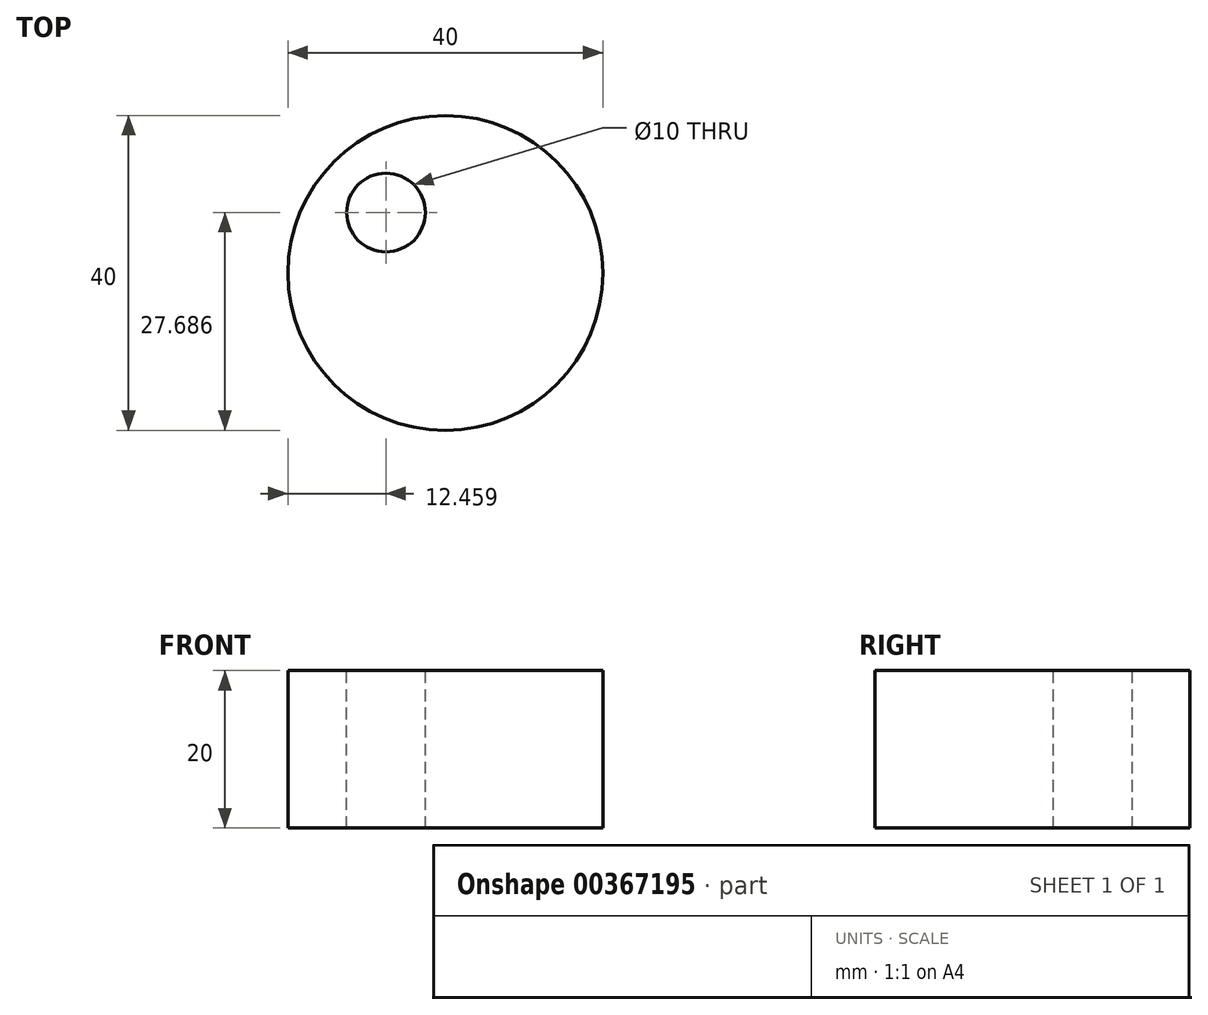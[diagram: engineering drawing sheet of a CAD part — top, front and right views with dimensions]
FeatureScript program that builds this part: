
annotation { "Feature Type Name" : "Feature", "Feature Type Description" : "" }
export const myFeature = defineFeature(function(context is Context, id is Id, definition is map)
    precondition{}
    {
        {
            var Q0;
            Q0=qCreatedBy(makeId("Front.planeOp"),FACE);
            var sketch = newSketch(context, id + "F0", { "sketchPlane" : qUnion([Q0])});
            skLineSegment(sketch, "E0.bottom", {"start": v(0, 0) * mm, "end": v(20, 0) * mm});
            skLineSegment(sketch, "E0.top", {"start": v(0, 20) * mm, "end": v(20, 20) * mm});
            skLineSegment(sketch, "E0.left", {"start": v(0, 0) * mm, "end": v(0, 20) * mm});
            skLineSegment(sketch, "E0.right", {"start": v(20, 0) * mm, "end": v(20, 20) * mm});
            skSolve(sketch);
        }
        {
            var Q0;
            Q0=makeQuery(id+"F0.imprint","IMPRINT",FACE,{"disambiguationData":[TD([[makeQuery(id+"F0.imprint","IMPRINT",EDGE,{"derivedFrom":sQuery(id+"F0.wireOp",EDGE,"E0.bottom")}),1.0]])]});
            var Q1;
            Q1=sQuery(id+"F0.wireOp",EDGE,"E0.left");
            revolve(context, id + "F1", {"entities" : qUnion([Q0]), "axis" : qUnion([Q1]), "revolveType" : RevolveType.FULL});
        }
        {
            var Q0;
            Q0=makeQuery(id+"F1.opRevolve","SWEPT_FACE",FACE,{"disambiguationData":[OSD([sQuery(id+"F0.wireOp",EDGE,"E0.top")])]});
            var sketch = newSketch(context, id + "F2", { "sketchPlane" : qUnion([Q0])});
            skCircle(sketch, "E1", {"center": v(-7.54, 7.69) * mm, "radius": 5 * mm});
            skSolve(sketch);
        }
        {
            var Q0;
            Q0=makeQuery(id+"F2.imprint","IMPRINT",FACE,{"disambiguationData":[TD([[makeQuery(id+"F2.imprint","IMPRINT",EDGE,{"derivedFrom":sQuery(id+"F2.wireOp",EDGE,"E1")}),1.0]])]});
            extrude(context, id + "F3", {"entities" : qUnion([Q0]), "operationType" : NewBodyOperationType.REMOVE, "oppositeDirection" : true, "depth" : 40 * mm});
        }
    });
